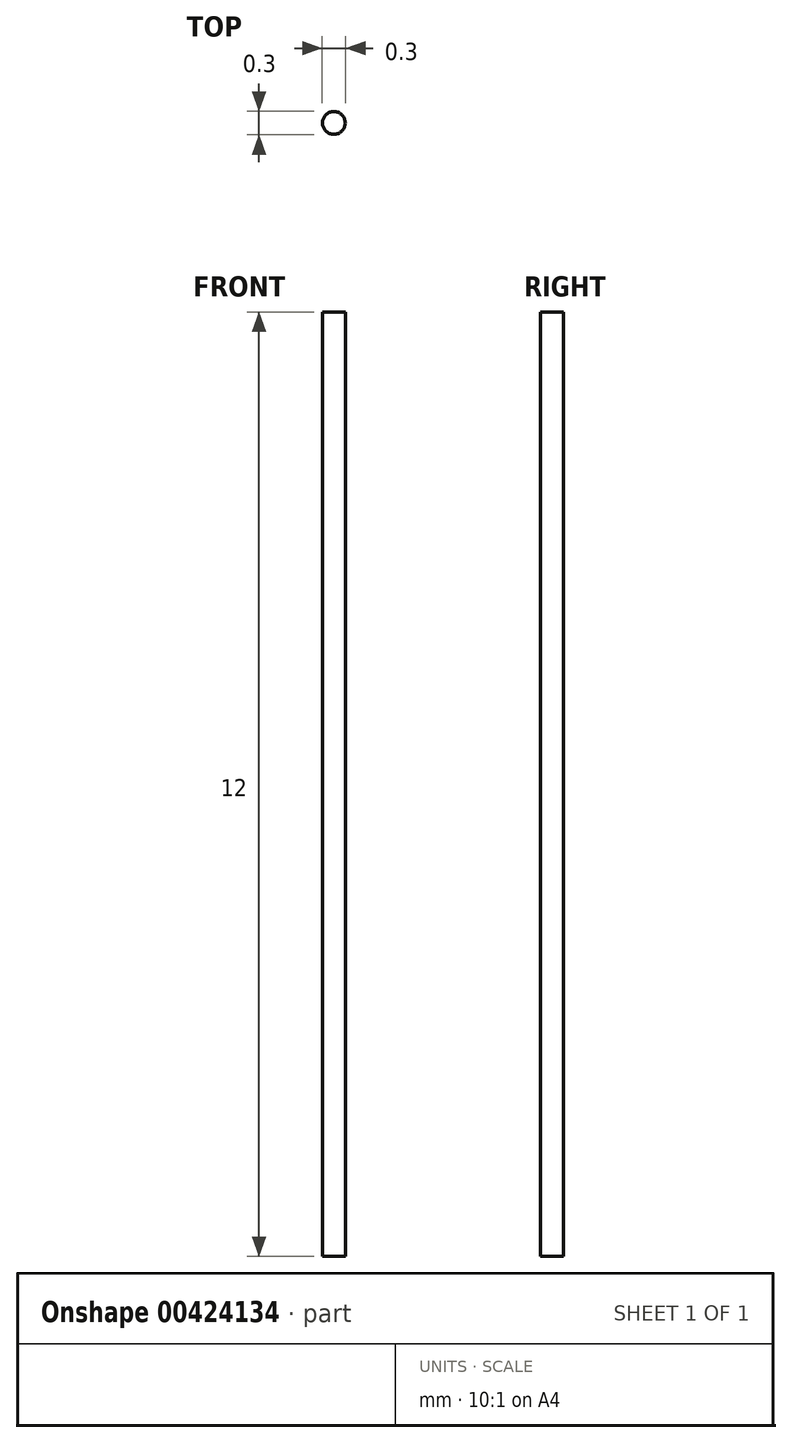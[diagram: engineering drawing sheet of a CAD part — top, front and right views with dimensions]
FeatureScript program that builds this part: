
annotation { "Feature Type Name" : "Feature", "Feature Type Description" : "" }
export const myFeature = defineFeature(function(context is Context, id is Id, definition is map)
    precondition{}
    {
        {
            var Q0;
            Q0=qCreatedBy(makeId("Top.planeOp"),FACE);
            var sketch = newSketch(context, id + "F0", { "sketchPlane" : qUnion([Q0])});
            skCircle(sketch, "E0", {"center": v(0, 0) * mm, "radius": 0.15 * mm});
            skSolve(sketch);
        }
        {
            var Q0;
            Q0 = qSketchRegion(id + "F0", true);
            extrude(context, id + "F1", {"entities" : qUnion([Q0]), "depth" : 12 * mm});
        }
    });
